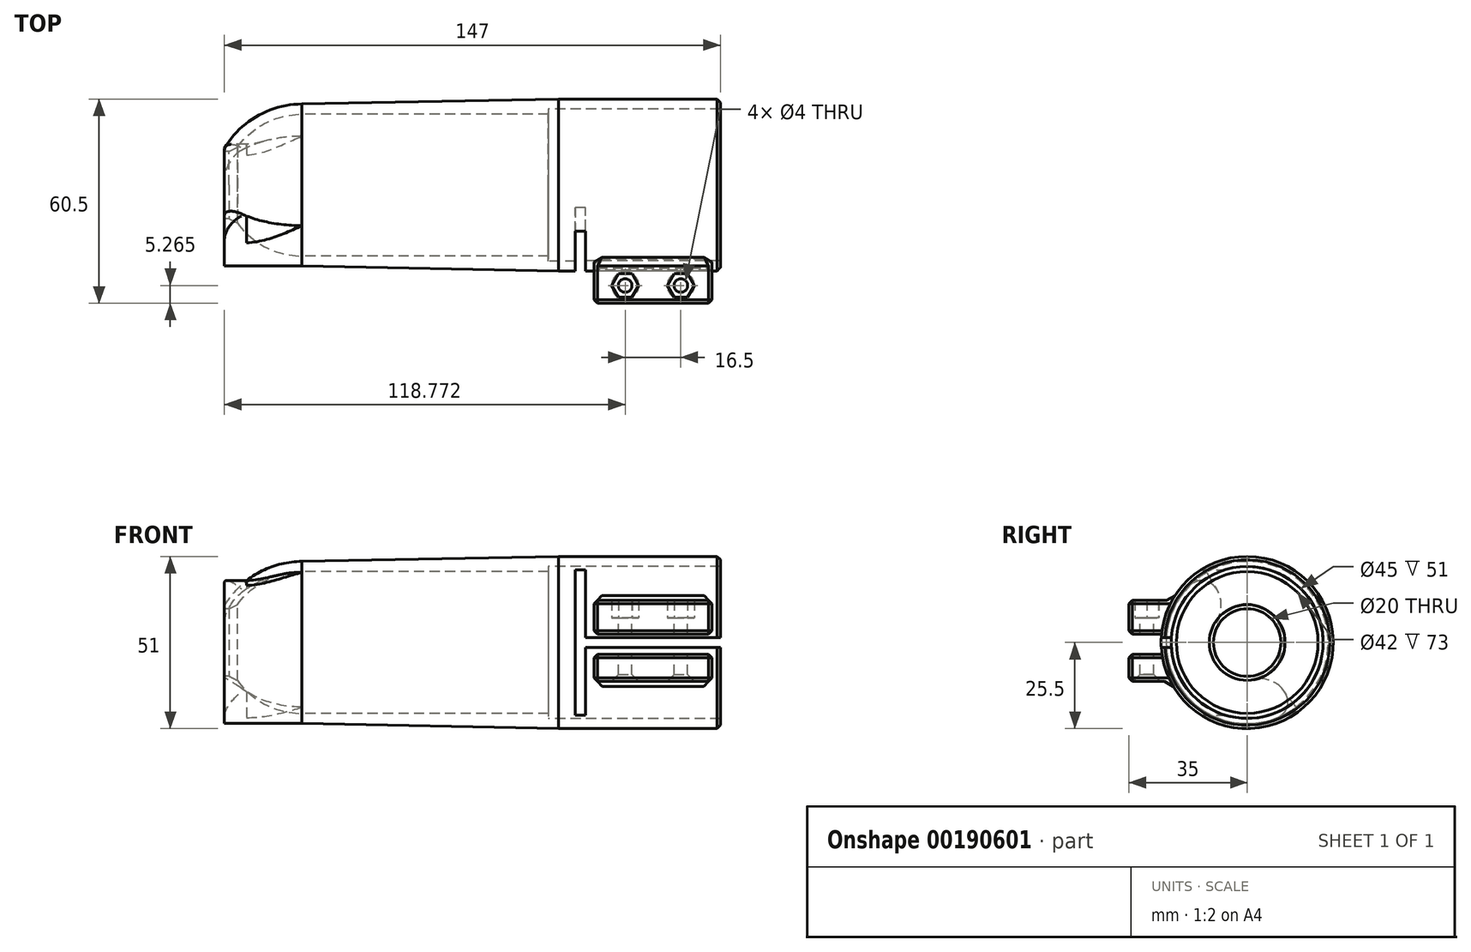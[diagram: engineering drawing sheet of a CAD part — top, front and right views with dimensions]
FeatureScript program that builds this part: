
annotation { "Feature Type Name" : "Feature", "Feature Type Description" : "" }
export const myFeature = defineFeature(function(context is Context, id is Id, definition is map)
    precondition{}
    {
        {
            var Q0;
            Q0=qCreatedBy(makeId("Front.planeOp"),FACE);
            var sketch = newSketch(context, id + "F0", { "sketchPlane" : qUnion([Q0])});
            skPoint(sketch, "E0", {"position": v(0, 0) * mm});
            skPoint(sketch, "E1", {"position": v(0, 21) * mm});
            skPoint(sketch, "E2", {"position": v(-20, 0) * mm});
            skPoint(sketch, "E3", {"position": v(-20, 10) * mm});
            skPoint(sketch, "E4", {"position": v(76, 21) * mm});
            skPoint(sketch, "E5", {"position": v(76, 0) * mm});
            skPoint(sketch, "E6", {"position": v(76, 22.5) * mm});
            skPoint(sketch, "E7", {"position": v(121, 0) * mm});
            skPoint(sketch, "E8", {"position": v(121, 22.5) * mm});
            skLineSegment(sketch, "E9", {"start": v(-20, 0) * mm, "end": v(121, 0) * mm});
            skLineSegment(sketch, "E10", {"start": v(76, 22.5) * mm, "end": v(121, 22.5) * mm});
            skArc(sketch, "E11", {"start": v(0, 21) * mm, "mid": v(-11.41, 18.07) * mm, "end": v(-20, 10) * mm});
            skArc(sketch, "E12.1", {"start": v(0, 24) * mm, "mid": v(-13.25, 20.48) * mm, "end": v(-23, 10.84) * mm});
            skLineSegment(sketch, "E13.1", {"start": v(76, 25.5) * mm, "end": v(124, 25.5) * mm});
            skLineSegment(sketch, "E14", {"start": v(0, 24) * mm, "end": v(76, 25.5) * mm});
            skPoint(sketch, "E15", {"position": v(-23, 10) * mm});
            skPoint(sketch, "E16", {"position": v(124, 22.5) * mm});
            skLineSegment(sketch, "E17", {"start": v(-23, 10) * mm, "end": v(-20, 10) * mm});
            skLineSegment(sketch, "E18", {"start": v(121, 22.5) * mm, "end": v(124, 22.5) * mm});
            skLineSegment(sketch, "E19", {"start": v(-23, 10.84) * mm, "end": v(-23, 10) * mm});
            skLineSegment(sketch, "E20", {"start": v(124, 25.5) * mm, "end": v(124, 22.5) * mm});
            skPoint(sketch, "E21", {"position": v(73, 21) * mm});
            skPoint(sketch, "E22", {"position": v(73, 25.44) * mm});
            skPoint(sketch, "E23", {"position": v(73, 22.5) * mm});
            skLineSegment(sketch, "E24", {"start": v(73, 21) * mm, "end": v(73, 22.5) * mm});
            skLineSegment(sketch, "E25", {"start": v(76, 22.5) * mm, "end": v(73, 22.5) * mm});
            skLineSegment(sketch, "E26", {"start": v(0, 21) * mm, "end": v(73, 21) * mm});
            skPoint(sketch, "E27", {"position": v(-23, 24) * mm});
            skLineSegment(sketch, "E28", {"start": v(-23, 24) * mm, "end": v(0, 24) * mm});
            skLineSegment(sketch, "E29", {"start": v(-23, 24) * mm, "end": v(-23, 10.84) * mm});
            skSolve(sketch);
        }
        {
            var Q0;
            Q0=makeQuery(id+"F0.imprint","IMPRINT",FACE,{"disambiguationData":[TD([[makeQuery(id+"F0.imprint","IMPRINT",EDGE,{"derivedFrom":sQuery(id+"F0.wireOp",EDGE,"E10")}),1.0]])]});
            var Q1;
            Q1=sQuery(id+"F0.wireOp",EDGE,"E9");
            revolve(context, id + "F1", {"entities" : qUnion([Q0]), "axis" : qUnion([Q1]), "revolveType" : RevolveType.FULL});
        }
        {
            var Q0;
            Q0=qCreatedBy(makeId("Front.planeOp"),FACE);
            var sketch = newSketch(context, id + "F2", { "sketchPlane" : qUnion([Q0])});
            skLineSegment(sketch, "E30", {"start": v(124, 0) * mm, "end": v(124, 1.5) * mm});
            skLineSegment(sketch, "E31", {"start": v(124, 1.5) * mm, "end": v(84, 1.5) * mm});
            skLineSegment(sketch, "E32", {"start": v(84, 1.5) * mm, "end": v(84, 21.5) * mm});
            skLineSegment(sketch, "E33", {"start": v(84, 21.5) * mm, "end": v(81, 21.5) * mm});
            skLineSegment(sketch, "E34", {"start": v(81, 21.5) * mm, "end": v(81, 0) * mm});
            skLineSegment(sketch, "E35.MirrorCS", {"start": v(78, 21.5) * mm, "end": v(81, 21.5) * mm});
            skLineSegment(sketch, "E36.MirrorCS", {"start": v(81, -21.5) * mm, "end": v(81, 0) * mm});
            skLineSegment(sketch, "E37.MirrorCS", {"start": v(84, -21.5) * mm, "end": v(81, -21.5) * mm});
            skLineSegment(sketch, "E38.MirrorCS", {"start": v(84, -1.5) * mm, "end": v(84, -21.5) * mm});
            skLineSegment(sketch, "E39.MirrorCS", {"start": v(124, -1.5) * mm, "end": v(84, -1.5) * mm});
            skLineSegment(sketch, "E40.MirrorCS", {"start": v(124, 0) * mm, "end": v(124, -1.5) * mm});
            skSolve(sketch);
        }
        {
            var Q0;
            Q0=makeQuery(id+"F2.imprint","IMPRINT",FACE,{"disambiguationData":[TD([[makeQuery(id+"F2.imprint","IMPRINT",EDGE,{"derivedFrom":sQuery(id+"F2.wireOp",EDGE,"E30")}),1.0]])]});
            extrude(context, id + "F3", {"entities" : qUnion([Q0]), "operationType" : NewBodyOperationType.REMOVE, "depth" : 39.5 * mm});
        }
        {
            var Q0;
            Q0=qCreatedBy(makeId("Front.planeOp"),FACE);
            var sketch = newSketch(context, id + "F4", { "sketchPlane" : qUnion([Q0])});
            skPoint(sketch, "E41", {"position": v(84.02, 0) * mm});
            skPoint(sketch, "E42", {"position": v(124.02, 0) * mm});
            skPoint(sketch, "E43", {"position": v(104.02, 0) * mm});
            skPoint(sketch, "E44", {"position": v(104.02, 7.5) * mm});
            skPoint(sketch, "E45", {"position": v(104.02, -7.5) * mm});
            skLineSegment(sketch, "E46.bottom", {"start": v(121.52, 12.5) * mm, "end": v(86.52, 12.5) * mm});
            skLineSegment(sketch, "E46.top", {"start": v(121.52, 2.5) * mm, "end": v(86.52, 2.5) * mm});
            skLineSegment(sketch, "E46.left", {"start": v(121.52, 12.5) * mm, "end": v(121.52, 2.5) * mm});
            skLineSegment(sketch, "E46.right", {"start": v(86.52, 12.5) * mm, "end": v(86.52, 2.5) * mm});
            skLineSegment(sketch, "E47.bottom", {"start": v(121.52, -11.5) * mm, "end": v(86.52, -11.5) * mm});
            skLineSegment(sketch, "E47.top", {"start": v(121.52, -3.5) * mm, "end": v(86.52, -3.5) * mm});
            skLineSegment(sketch, "E47.left", {"start": v(121.52, -11.5) * mm, "end": v(121.52, -3.5) * mm});
            skLineSegment(sketch, "E47.right", {"start": v(86.52, -11.5) * mm, "end": v(86.52, -3.5) * mm});
            skSolve(sketch);
        }
        {
            var Q0;
            Q0=makeQuery(id+"F4.imprint","IMPRINT",FACE,{"disambiguationData":[TD([[makeQuery(id+"F4.imprint","IMPRINT",EDGE,{"derivedFrom":sQuery(id+"F4.wireOp",EDGE,"E46.bottom")}),1.0]])]});
            var Q1;
            Q1=makeQuery(id+"F4.imprint","IMPRINT",FACE,{"disambiguationData":[TD([[makeQuery(id+"F4.imprint","IMPRINT",EDGE,{"derivedFrom":sQuery(id+"F4.wireOp",EDGE,"E47.bottom")}),-1.0]])]});
            extrude(context, id + "F5", {"entities" : qUnion([Q0, Q1]), "operationType" : NewBodyOperationType.ADD, "depth" : 35 * mm});
        }
        {
            var Q0;
            {var subQ1=sQuery(id+"F4.wireOp",EDGE,"E46.left");Q0=makeQuery(id+"F5.boolean.opBoolean","SPLIT",FACE,{"disambiguationData":[TD([makeQuery(id+"F1.opRevolve","SWEPT_FACE",FACE,{"disambiguationData":[OSD([sQuery(id+"F0.wireOp",EDGE,"E10"),sQuery(id+"F0.wireOp",EDGE,"E18")])]})])],"derivedFrom":makeQuery(id+"F5.opExtrude","SWEPT_FACE",FACE,{"disambiguationData":[OSD([subQ1])]})});}
            var Q1;
            {var subQ1=sQuery(id+"F4.wireOp",EDGE,"E47.left");Q1=makeQuery(id+"F5.boolean.opBoolean","SPLIT",FACE,{"disambiguationData":[TD([makeQuery(id+"F1.opRevolve","SWEPT_FACE",FACE,{"disambiguationData":[OSD([sQuery(id+"F0.wireOp",EDGE,"E10"),sQuery(id+"F0.wireOp",EDGE,"E18")])]})])],"derivedFrom":makeQuery(id+"F5.opExtrude","SWEPT_FACE",FACE,{"disambiguationData":[OSD([subQ1])]})});}
            extrude(context, id + "F6", {"entities" : qUnion([Q0, Q1]), "operationType" : NewBodyOperationType.REMOVE, "oppositeDirection" : true, "depth" : 40 * mm});
        }
        {
            var Q0;
            Q0=makeQuery(id+"F5.opExtrude","CAP_EDGE",EDGE,{"disambiguationData":[OSD([sQuery(id+"F4.wireOp",EDGE,"E46.bottom")])],"isStart":false});
            var Q1;
            {var subQ0=sQuery(id+"F4.wireOp",EDGE,"E46.bottom");var subQ1=sQuery(id+"F4.wireOp",EDGE,"E46.right");Q1=makeQuery(id+"F5.boolean.opBoolean","SPLIT",EDGE,{"disambiguationData":[TD([makeQuery(id+"F1.opRevolve","SWEPT_FACE",FACE,{"disambiguationData":[OSD([sQuery(id+"F0.wireOp",EDGE,"E13.1")])]})])],"derivedFrom":makeQuery(id+"F5.opExtrude","SWEPT_EDGE",EDGE,{"disambiguationData":[OSD([subQ0,subQ1])]})});}
            var Q2;
            {var subQ0=sQuery(id+"F4.wireOp",EDGE,"E46.bottom");var subQ1=sQuery(id+"F4.wireOp",EDGE,"E46.left");Q2=makeQuery(id+"F5.boolean.opBoolean","SPLIT",EDGE,{"disambiguationData":[TD([makeQuery(id+"F1.opRevolve","SWEPT_FACE",FACE,{"disambiguationData":[OSD([sQuery(id+"F0.wireOp",EDGE,"E13.1")])]})])],"derivedFrom":makeQuery(id+"F5.opExtrude","SWEPT_EDGE",EDGE,{"disambiguationData":[OSD([subQ0,subQ1])]})});}
            var Q3;
            Q3=makeQuery(id+"F5.opExtrude","CAP_EDGE",EDGE,{"disambiguationData":[OSD([sQuery(id+"F4.wireOp",EDGE,"E46.left")])],"isStart":false});
            var Q4;
            Q4=makeQuery(id+"F5.opExtrude","CAP_EDGE",EDGE,{"disambiguationData":[OSD([sQuery(id+"F4.wireOp",EDGE,"E46.right")])],"isStart":false});
            var Q5;
            {var subQ0=sQuery(id+"F4.wireOp",EDGE,"E46.left");var subQ1=sQuery(id+"F4.wireOp",EDGE,"E46.top");Q5=makeQuery(id+"F5.boolean.opBoolean","SPLIT",EDGE,{"disambiguationData":[TD([makeQuery(id+"F1.opRevolve","SWEPT_FACE",FACE,{"disambiguationData":[OSD([sQuery(id+"F0.wireOp",EDGE,"E13.1")])]})])],"derivedFrom":makeQuery(id+"F5.opExtrude","SWEPT_EDGE",EDGE,{"disambiguationData":[OSD([subQ1,subQ0])]})});}
            var Q6;
            Q6=makeQuery(id+"F5.opExtrude","CAP_EDGE",EDGE,{"disambiguationData":[OSD([sQuery(id+"F4.wireOp",EDGE,"E46.top")])],"isStart":false});
            var Q7;
            {var subQ0=sQuery(id+"F4.wireOp",EDGE,"E46.right");var subQ1=sQuery(id+"F4.wireOp",EDGE,"E46.top");Q7=makeQuery(id+"F5.boolean.opBoolean","SPLIT",EDGE,{"disambiguationData":[TD([makeQuery(id+"F1.opRevolve","SWEPT_FACE",FACE,{"disambiguationData":[OSD([sQuery(id+"F0.wireOp",EDGE,"E13.1")])]})])],"derivedFrom":makeQuery(id+"F5.opExtrude","SWEPT_EDGE",EDGE,{"disambiguationData":[OSD([subQ1,subQ0])]})});}
            var Q8;
            Q8=makeQuery(id+"F5.opExtrude","CAP_EDGE",EDGE,{"disambiguationData":[OSD([sQuery(id+"F4.wireOp",EDGE,"E47.bottom")])],"isStart":false});
            var Q9;
            {var subQ0=sQuery(id+"F4.wireOp",EDGE,"E47.bottom");var subQ1=sQuery(id+"F4.wireOp",EDGE,"E47.right");Q9=makeQuery(id+"F5.boolean.opBoolean","SPLIT",EDGE,{"disambiguationData":[TD([makeQuery(id+"F1.opRevolve","SWEPT_FACE",FACE,{"disambiguationData":[OSD([sQuery(id+"F0.wireOp",EDGE,"E13.1")])]})])],"derivedFrom":makeQuery(id+"F5.opExtrude","SWEPT_EDGE",EDGE,{"disambiguationData":[OSD([subQ0,subQ1])]})});}
            var Q10;
            {var subQ0=sQuery(id+"F4.wireOp",EDGE,"E47.bottom");var subQ1=sQuery(id+"F4.wireOp",EDGE,"E47.left");Q10=makeQuery(id+"F5.boolean.opBoolean","SPLIT",EDGE,{"disambiguationData":[TD([makeQuery(id+"F1.opRevolve","SWEPT_FACE",FACE,{"disambiguationData":[OSD([sQuery(id+"F0.wireOp",EDGE,"E13.1")])]})])],"derivedFrom":makeQuery(id+"F5.opExtrude","SWEPT_EDGE",EDGE,{"disambiguationData":[OSD([subQ0,subQ1])]})});}
            var Q11;
            Q11=makeQuery(id+"F5.opExtrude","CAP_EDGE",EDGE,{"disambiguationData":[OSD([sQuery(id+"F4.wireOp",EDGE,"E47.left")])],"isStart":false});
            var Q12;
            Q12=makeQuery(id+"F5.opExtrude","CAP_EDGE",EDGE,{"disambiguationData":[OSD([sQuery(id+"F4.wireOp",EDGE,"E47.right")])],"isStart":false});
            var Q13;
            {var subQ0=sQuery(id+"F4.wireOp",EDGE,"E47.left");var subQ1=sQuery(id+"F4.wireOp",EDGE,"E47.top");Q13=makeQuery(id+"F5.boolean.opBoolean","SPLIT",EDGE,{"disambiguationData":[TD([makeQuery(id+"F1.opRevolve","SWEPT_FACE",FACE,{"disambiguationData":[OSD([sQuery(id+"F0.wireOp",EDGE,"E13.1")])]})])],"derivedFrom":makeQuery(id+"F5.opExtrude","SWEPT_EDGE",EDGE,{"disambiguationData":[OSD([subQ1,subQ0])]})});}
            var Q14;
            Q14=makeQuery(id+"F5.opExtrude","CAP_EDGE",EDGE,{"disambiguationData":[OSD([sQuery(id+"F4.wireOp",EDGE,"E47.top")])],"isStart":false});
            var Q15;
            {var subQ0=sQuery(id+"F4.wireOp",EDGE,"E47.right");var subQ1=sQuery(id+"F4.wireOp",EDGE,"E47.top");Q15=makeQuery(id+"F5.boolean.opBoolean","SPLIT",EDGE,{"disambiguationData":[TD([makeQuery(id+"F1.opRevolve","SWEPT_FACE",FACE,{"disambiguationData":[OSD([sQuery(id+"F0.wireOp",EDGE,"E13.1")])]})])],"derivedFrom":makeQuery(id+"F5.opExtrude","SWEPT_EDGE",EDGE,{"disambiguationData":[OSD([subQ1,subQ0])]})});}
            var Q16;
            Q16=makeQuery(id+"F1.opRevolve","SWEPT_EDGE",EDGE,{"disambiguationData":[OSD([sQuery(id+"F0.wireOp",EDGE,"E13.1"),sQuery(id+"F0.wireOp",EDGE,"E20")])]});
            chamfer(context, id + "F7", {"entities" : qUnion([Q0, Q1, Q2, Q3, Q4, Q5, Q6, Q7, Q8, Q9, Q10, Q11, Q12, Q13, Q14, Q15, Q16]), "width" : 1 * mm, "tangentPropagation" : true});
        }
        {
            var Q0;
            Q0=qCreatedBy(makeId("Top.planeOp"),FACE);
            var sketch = newSketch(context, id + "F8", { "sketchPlane" : qUnion([Q0])});
            skPoint(sketch, "E48", {"position": v(87.52, -25.46) * mm});
            skPoint(sketch, "E49", {"position": v(120.52, -25.46) * mm});
            skPoint(sketch, "E50", {"position": v(120.52, -34) * mm});
            skPoint(sketch, "E51", {"position": v(87.52, -34) * mm});
            skLineSegment(sketch, "E52", {"start": v(87.52, -34) * mm, "end": v(120.52, -34) * mm, "construction": true});
            skLineSegment(sketch, "E53", {"start": v(87.52, -34) * mm, "end": v(87.52, -25.46) * mm, "construction": true});
            skPoint(sketch, "E54", {"position": v(104.02, -25.46) * mm});
            skPoint(sketch, "E55", {"position": v(104.02, -34) * mm});
            skLineSegment(sketch, "E56", {"start": v(120.52, -25.46) * mm, "end": v(120.52, -34) * mm, "construction": true});
            skPoint(sketch, "E57", {"position": v(87.52, -29.74) * mm});
            skPoint(sketch, "E58", {"position": v(120.52, -29.74) * mm});
            skPoint(sketch, "E59", {"position": v(104.02, -29.74) * mm});
            skPoint(sketch, "E60", {"position": v(95.77, -29.74) * mm});
            skPoint(sketch, "E61", {"position": v(112.27, -29.74) * mm});
            skCircle(sketch, "E62", {"center": v(95.77, -29.74) * mm, "radius": 2 * mm});
            skCircle(sketch, "E63", {"center": v(112.27, -29.74) * mm, "radius": 2 * mm});
            skSolve(sketch);
        }
        {
            var Q0;
            Q0=makeQuery(id+"F8.imprint","IMPRINT",FACE,{"disambiguationData":[TD([[makeQuery(id+"F8.imprint","IMPRINT",EDGE,{"derivedFrom":sQuery(id+"F8.wireOp",EDGE,"E62")}),1.0]])]});
            var Q1;
            Q1=makeQuery(id+"F8.imprint","IMPRINT",FACE,{"disambiguationData":[TD([[makeQuery(id+"F8.imprint","IMPRINT",EDGE,{"derivedFrom":sQuery(id+"F8.wireOp",EDGE,"E63")}),1.0]])]});
            extrude(context, id + "F9", {"entities" : qUnion([Q0, Q1]), "operationType" : NewBodyOperationType.REMOVE, "oppositeDirection" : true, "depth" : 35 * mm, "symmetric" : true});
        }
        {
            var Q0;
            Q0=qCreatedBy(makeId("Top.planeOp"),FACE);
            var sketch = newSketch(context, id + "F10", { "sketchPlane" : qUnion([Q0])});
            skPoint(sketch, "E64", {"position": v(95.78, -29.73) * mm});
            skPoint(sketch, "E65", {"position": v(112.27, -29.73) * mm});
            skLineSegment(sketch, "E66.0", {"start": v(93.75, -33.23) * mm, "end": v(91.73, -29.73) * mm});
            skLineSegment(sketch, "E66.1", {"start": v(91.73, -29.73) * mm, "end": v(93.76, -26.23) * mm});
            skLineSegment(sketch, "E66.2", {"start": v(93.76, -26.23) * mm, "end": v(97.8, -26.24) * mm});
            skLineSegment(sketch, "E66.3", {"start": v(97.8, -26.24) * mm, "end": v(99.82, -29.74) * mm});
            skLineSegment(sketch, "E66.4", {"start": v(99.82, -29.74) * mm, "end": v(97.8, -33.24) * mm});
            skLineSegment(sketch, "E66.5", {"start": v(97.8, -33.24) * mm, "end": v(93.75, -33.23) * mm});
            skPoint(sketch, "E66.0.midPoint", {"position": v(92.74, -31.48) * mm});
            skLineSegment(sketch, "E67.0", {"start": v(110.25, -33.23) * mm, "end": v(108.23, -29.73) * mm});
            skLineSegment(sketch, "E67.1", {"start": v(108.23, -29.73) * mm, "end": v(110.26, -26.23) * mm});
            skLineSegment(sketch, "E67.2", {"start": v(110.26, -26.23) * mm, "end": v(114.3, -26.24) * mm});
            skLineSegment(sketch, "E67.3", {"start": v(114.3, -26.24) * mm, "end": v(116.31, -29.74) * mm});
            skLineSegment(sketch, "E67.4", {"start": v(116.31, -29.74) * mm, "end": v(114.29, -33.24) * mm});
            skLineSegment(sketch, "E67.5", {"start": v(114.29, -33.24) * mm, "end": v(110.25, -33.23) * mm});
            skPoint(sketch, "E67.0.midPoint", {"position": v(109.24, -31.48) * mm});
            skSolve(sketch);
        }
        {
            var Q0;
            Q0=makeQuery(id+"F10.imprint","IMPRINT",FACE,{"disambiguationData":[TD([[makeQuery(id+"F10.imprint","IMPRINT",EDGE,{"derivedFrom":sQuery(id+"F10.wireOp",EDGE,"E67.0")}),-1.0]])]});
            var Q1;
            Q1=makeQuery(id+"F10.imprint","IMPRINT",FACE,{"disambiguationData":[TD([[makeQuery(id+"F10.imprint","IMPRINT",EDGE,{"derivedFrom":sQuery(id+"F10.wireOp",EDGE,"E66.0")}),-1.0]])]});
            extrude(context, id + "F11", {"entities" : qUnion([Q0, Q1]), "operationType" : NewBodyOperationType.REMOVE, "depth" : 14.9 * mm, "hasSecondDirection" : true, "secondDirectionOppositeDirection" : false, "secondDirectionDepth" : 7.3 * mm});
        }
        {
            var Q0;
            Q0=makeQuery(id+"F5.boolean.opBoolean","INTERSECT",EDGE,{"derivedFrom":[makeQuery(id+"F1.opRevolve","SWEPT_FACE",FACE,{"disambiguationData":[OSD([sQuery(id+"F0.wireOp",EDGE,"E13.1")])]}),makeQuery(id+"F5.opExtrude","SWEPT_FACE",FACE,{"disambiguationData":[OSD([sQuery(id+"F4.wireOp",EDGE,"E47.bottom")])]})]});
            var Q1;
            Q1=makeQuery(id+"F5.boolean.opBoolean","INTERSECT",EDGE,{"derivedFrom":[makeQuery(id+"F1.opRevolve","SWEPT_FACE",FACE,{"disambiguationData":[OSD([sQuery(id+"F0.wireOp",EDGE,"E13.1")])]}),makeQuery(id+"F5.opExtrude","SWEPT_FACE",FACE,{"disambiguationData":[OSD([sQuery(id+"F4.wireOp",EDGE,"E46.bottom")])]})]});
            chamfer(context, id + "F12", {"entities" : qUnion([Q0, Q1]), "width" : 3 * mm, "tangentPropagation" : true});
        }
        {
            var Q0;
            {var subQ2=sQuery(id+"F4.wireOp",EDGE,"E47.bottom");Q0=makeQuery(id+"F9.boolean.opBoolean","INTERSECT",EDGE,{"derivedFrom":[makeQuery(id+"F5.boolean.opBoolean","SPLIT",FACE,{"disambiguationData":[TD([makeQuery(id+"F1.opRevolve","SWEPT_FACE",FACE,{"disambiguationData":[OSD([sQuery(id+"F0.wireOp",EDGE,"E13.1")])]})])],"derivedFrom":makeQuery(id+"F5.opExtrude","SWEPT_FACE",FACE,{"disambiguationData":[OSD([subQ2])]})}),makeQuery(id+"F9.opExtrude","SWEPT_FACE",FACE,{"disambiguationData":[OSD([sQuery(id+"F8.wireOp",EDGE,"E63")])]})]});}
            var Q1;
            {var subQ2=sQuery(id+"F4.wireOp",EDGE,"E47.bottom");Q1=makeQuery(id+"F9.boolean.opBoolean","INTERSECT",EDGE,{"derivedFrom":[makeQuery(id+"F5.boolean.opBoolean","SPLIT",FACE,{"disambiguationData":[TD([makeQuery(id+"F1.opRevolve","SWEPT_FACE",FACE,{"disambiguationData":[OSD([sQuery(id+"F0.wireOp",EDGE,"E13.1")])]})])],"derivedFrom":makeQuery(id+"F5.opExtrude","SWEPT_FACE",FACE,{"disambiguationData":[OSD([subQ2])]})}),makeQuery(id+"F9.opExtrude","SWEPT_FACE",FACE,{"disambiguationData":[OSD([sQuery(id+"F8.wireOp",EDGE,"E62")])]})]});}
            chamfer(context, id + "F13", {"entities" : qUnion([Q0, Q1]), "width" : 2 * mm, "tangentPropagation" : true});
        }
        {
            var Q0;
            Q0=makeQuery(id+"F0.imprint","IMPRINT",FACE,{"disambiguationData":[TD([[makeQuery(id+"F0.imprint","IMPRINT",EDGE,{"derivedFrom":sQuery(id+"F0.wireOp",EDGE,"E12.1")}),-1.0]])]});
            var Q1;
            Q1=sQuery(id+"F0.wireOp",EDGE,"E9");
            revolve(context, id + "F14", {"operationType" : NewBodyOperationType.ADD, "entities" : qUnion([Q0]), "axis" : qUnion([Q1]), "revolveType" : RevolveType.TWO_DIRECTIONS, "angle" : 217.1 * degree, "angleBack" : 30 * degree});
        }
        {
            var Q0;
            Q0=makeQuery(id+"F14.opRevolve","CAP_EDGE",EDGE,{"disambiguationData":[OSD([sQuery(id+"F0.wireOp",EDGE,"E29")])],"isStart":true});
            var Q1;
            Q1=makeQuery(id+"F14.opRevolve","CAP_EDGE",EDGE,{"disambiguationData":[OSD([sQuery(id+"F0.wireOp",EDGE,"E29")])],"isStart":false});
            var Q2;
            Q2=makeQuery(id+"F14.opRevolve","CAP_EDGE",EDGE,{"disambiguationData":[OSD([sQuery(id+"F0.wireOp",EDGE,"E28")])],"isStart":true});
            var Q3;
            Q3=makeQuery(id+"F14.opRevolve","CAP_EDGE",EDGE,{"disambiguationData":[OSD([sQuery(id+"F0.wireOp",EDGE,"E28")])],"isStart":false});
            fillet(context, id + "F15", {"entities" : qUnion([Q0, Q1, Q2, Q3]), "radius" : 5 * mm, "tangentPropagation" : true, "allowEdgeOverflow" : false});
        }
        {
            var Q0;
            Q0=makeQuery(id+"F1.opRevolve","SWEPT_EDGE",EDGE,{"disambiguationData":[OSD([sQuery(id+"F0.wireOp",EDGE,"E11"),sQuery(id+"F0.wireOp",EDGE,"E17")])]});
            chamfer(context, id + "F16", {"entities" : qUnion([Q0]), "width" : 3 * mm, "tangentPropagation" : true});
        }
    });
